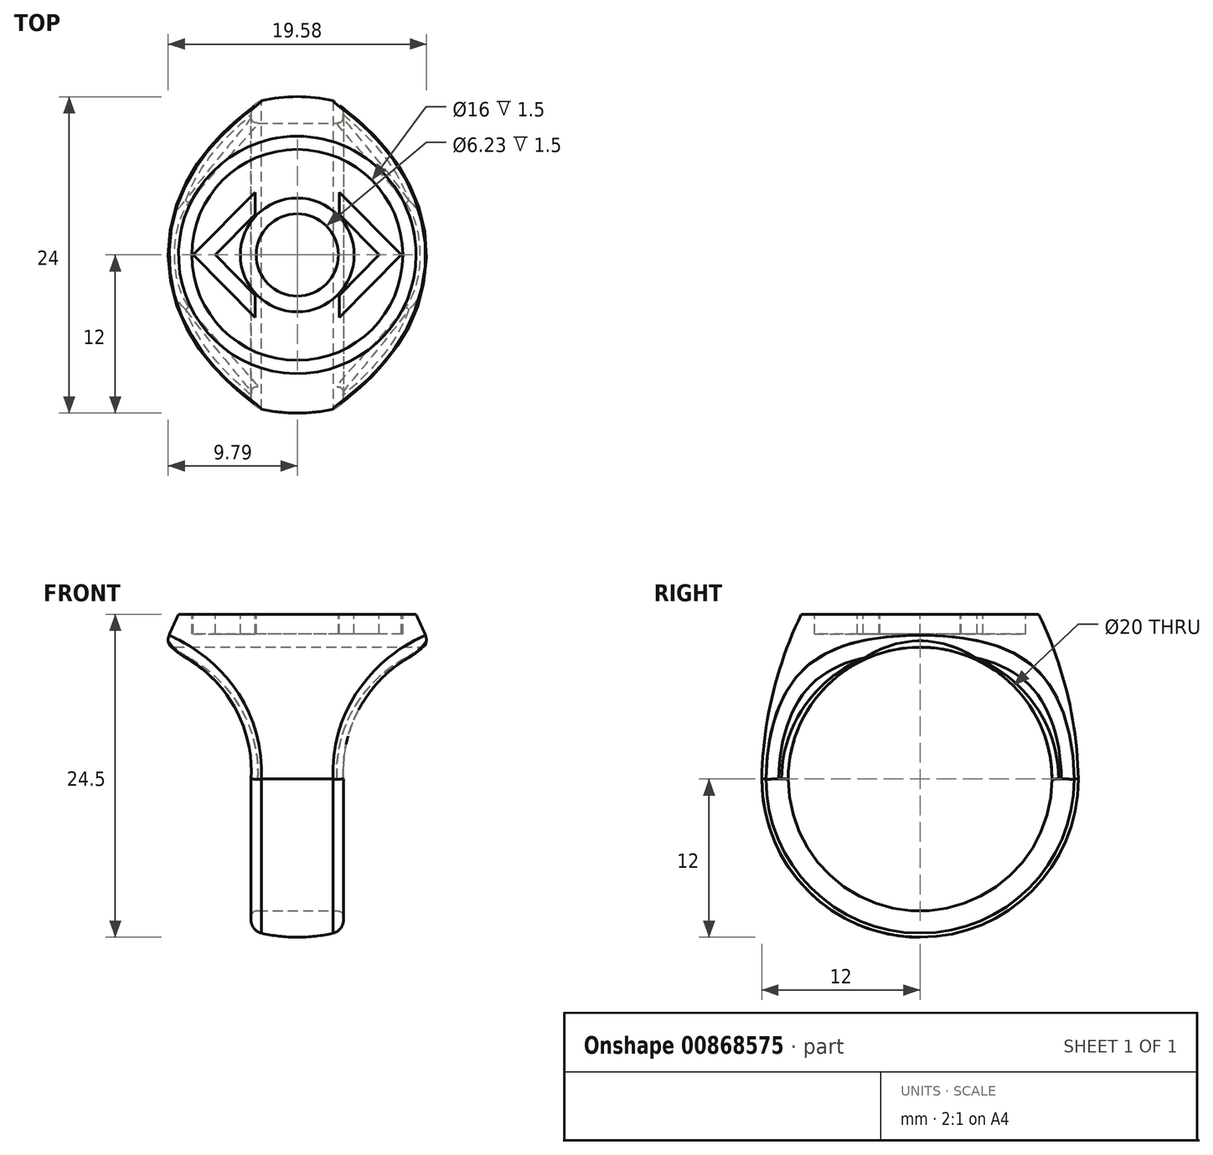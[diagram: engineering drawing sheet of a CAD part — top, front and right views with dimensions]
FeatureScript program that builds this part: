
annotation { "Feature Type Name" : "Feature", "Feature Type Description" : "" }
export const myFeature = defineFeature(function(context is Context, id is Id, definition is map)
    precondition{}
    {
        {
            var Q0;
            Q0=qCreatedBy(makeId("Right.planeOp"),FACE);
            var sketch = newSketch(context, id + "F0", { "sketchPlane" : qUnion([Q0])});
            skLineSegment(sketch, "E0", {"start": v(0, 0) * mm, "end": v(0, -24.5) * mm});
            skLineSegment(sketch, "E1", {"start": v(0, 0) * mm, "end": v(-9, 0) * mm});
            skArc(sketch, "E2", {"start": v(-12, -12.5) * mm, "mid": v(-8.49, -20.99) * mm, "end": v(0, -24.5) * mm});
            skLineSegment(sketch, "E3", {"start": v(0, -12.5) * mm, "end": v(-12, -12.5) * mm, "construction": true});
            skArc(sketch, "E4", {"start": v(-9, 0) * mm, "mid": v(-11.18, -6.09) * mm, "end": v(-12, -12.5) * mm});
            skSolve(sketch);
        }
        {
            var Q0;
            Q0=makeQuery(id+"F0.imprint","IMPRINT",FACE,{"disambiguationData":[TD([[makeQuery(id+"F0.imprint","IMPRINT",EDGE,{"derivedFrom":sQuery(id+"F0.wireOp",EDGE,"E0")}),-1.0]])]});
            var Q1;
            Q1=sQuery(id+"F0.wireOp",EDGE,"E0");
            revolve(context, id + "F1", {"entities" : qUnion([Q0]), "axis" : qUnion([Q1]), "revolveType" : RevolveType.FULL});
        }
        {
            var Q0;
            Q0=qCreatedBy(makeId("Right.planeOp"),FACE);
            var sketch = newSketch(context, id + "F2", { "sketchPlane" : qUnion([Q0])});
            skCircle(sketch, "E5", {"center": v(0, -12.5) * mm, "radius": 10 * mm});
            skSolve(sketch);
        }
        {
            var Q0;
            Q0=qSketchRegion(id+"F2",true);
            extrude(context, id + "F3", {"entities" : qUnion([Q0]), "operationType" : NewBodyOperationType.REMOVE, "endBound" : BoundingType.SYMMETRIC, "oppositeDirection" : true, "depth" : 25 * mm, "offsetDistance" : 25 * mm});
        }
        {
            var Q0;
            Q0=qCreatedBy(makeId("Front.planeOp"),FACE);
            var sketch = newSketch(context, id + "F4", { "sketchPlane" : qUnion([Q0])});
            skLineSegment(sketch, "E6", {"start": v(3.5, -26.5) * mm, "end": v(3.5, -12.5) * mm});
            skArc(sketch, "E7", {"start": v(10.15, -2.5) * mm, "mid": v(5.16, -6.39) * mm, "end": v(3.5, -12.5) * mm});
            skLineSegment(sketch, "E8", {"start": v(10.15, -2.5) * mm, "end": v(11.65, -2.5) * mm});
            skLineSegment(sketch, "E9", {"start": v(11.65, -2.5) * mm, "end": v(11.65, -26.5) * mm});
            skLineSegment(sketch, "E10", {"start": v(11.65, -26.5) * mm, "end": v(3.5, -26.5) * mm});
            skPoint(sketch, "E11.start.orphan", {"position": v(0, -24.5) * mm});
            skLineSegment(sketch, "E12", {"start": v(0, 0) * mm, "end": v(0, -24.5) * mm, "construction": true});
            skLineSegment(sketch, "E13.MirrorCS", {"start": v(-3.5, -26.5) * mm, "end": v(-3.5, -12.5) * mm});
            skArc(sketch, "E14.MirrorCS", {"start": v(-10.15, -2.5) * mm, "mid": v(-5.16, -6.39) * mm, "end": v(-3.5, -12.5) * mm});
            skLineSegment(sketch, "E15.MirrorCS", {"start": v(-11.65, -2.5) * mm, "end": v(-11.65, -26.5) * mm});
            skLineSegment(sketch, "E16.MirrorCS", {"start": v(-11.65, -26.5) * mm, "end": v(-3.5, -26.5) * mm});
            skLineSegment(sketch, "E17.MirrorCS", {"start": v(-10.15, -2.5) * mm, "end": v(-11.65, -2.5) * mm});
            skSolve(sketch);
        }
        {
            var Q0;
            Q0=qSketchRegion(id+"F4",true);
            extrude(context, id + "F5", {"entities" : qUnion([Q0]), "operationType" : NewBodyOperationType.REMOVE, "endBound" : BoundingType.SYMMETRIC, "depth" : 25 * mm, "offsetDistance" : 25 * mm});
        }
        {
            var Q0;
            Q0=makeQuery(id+"F1.opRevolve","SWEPT_FACE",FACE,{"disambiguationData":[OSD([sQuery(id+"F0.wireOp",EDGE,"E1")])]});
            var sketch = newSketch(context, id + "F6", { "sketchPlane" : qUnion([Q0])});
            skCircle(sketch, "E18", {"center": v(0, 0) * mm, "radius": 8 * mm});
            skLineSegment(sketch, "E19", {"start": v(-8, 0) * mm, "end": v(8, 0) * mm, "construction": true});
            skArc(sketch, "E20", {"start": v(3.11, 0) * mm, "mid": v(0, 3.11) * mm, "end": v(-3.11, 0) * mm});
            skArc(sketch, "E21", {"start": v(4.31, 0) * mm, "mid": v(0, 4.31) * mm, "end": v(-4.31, 0) * mm});
            skLineSegment(sketch, "E22", {"start": v(0, 8) * mm, "end": v(0, -8) * mm, "construction": true});
            skArc(sketch, "E23", {"start": v(4.31, 0) * mm, "mid": v(0, -4.31) * mm, "end": v(-4.31, 0) * mm});
            skArc(sketch, "E24", {"start": v(3.11, 0) * mm, "mid": v(0, -3.11) * mm, "end": v(-3.11, 0) * mm});
            skLineSegment(sketch, "E25", {"start": v(3.18, 4.76) * mm, "end": v(3.18, 3.05) * mm});
            skLineSegment(sketch, "E26", {"start": v(6.21, 0) * mm, "end": v(3.18, -3.05) * mm});
            skLineSegment(sketch, "E27", {"start": v(6.21, 0) * mm, "end": v(3.18, 3.05) * mm});
            skLineSegment(sketch, "E28.trimOffspring", {"start": v(3.18, -3.05) * mm, "end": v(3.18, -4.76) * mm});
            skLineSegment(sketch, "E29", {"start": v(3.18, -4.76) * mm, "end": v(7.9, 0) * mm});
            skLineSegment(sketch, "E30", {"start": v(7.9, 0) * mm, "end": v(3.18, 4.76) * mm});
            skLineSegment(sketch, "E31.MirrorCS", {"start": v(-3.18, 4.76) * mm, "end": v(-3.18, 3.05) * mm});
            skLineSegment(sketch, "E32.MirrorCS", {"start": v(-7.9, 0) * mm, "end": v(-3.18, 4.76) * mm});
            skLineSegment(sketch, "E33.MirrorCS", {"start": v(-6.21, 0) * mm, "end": v(-3.18, 3.05) * mm});
            skLineSegment(sketch, "E34.MirrorCS", {"start": v(-6.21, 0) * mm, "end": v(-3.18, -3.05) * mm});
            skLineSegment(sketch, "E35.MirrorCS", {"start": v(-3.18, -4.76) * mm, "end": v(-7.9, 0) * mm});
            skLineSegment(sketch, "E36.MirrorCS", {"start": v(-3.18, -3.05) * mm, "end": v(-3.18, -4.76) * mm});
            skSolve(sketch);
        }
        {
            var Q0;
            Q0=makeQuery(id+"F6.imprint","IMPRINT",FACE,{"disambiguationData":[TD([[makeQuery(id+"F6.imprint","IMPRINT",EDGE,{"derivedFrom":sQuery(id+"F6.wireOp",EDGE,"E20")}),1.0]])]});
            var Q1;
            Q1=makeQuery(id+"F6.imprint","IMPRINT",FACE,{"disambiguationData":[TD([[makeQuery(id+"F6.imprint","IMPRINT",EDGE,{"derivedFrom":sQuery(id+"F6.wireOp",EDGE,"E18")}),1.0]])]});
            extrude(context, id + "F7", {"entities" : qUnion([Q0, Q1]), "operationType" : NewBodyOperationType.REMOVE, "oppositeDirection" : true, "depth" : 1.5 * mm, "offsetDistance" : 25 * mm});
        }
        {
            var Q0;
            Q0=makeQuery(id+"F5.boolean.opBoolean","INTERSECT",EDGE,{"disambiguationData":[OD(1.0)],"derivedFrom":[makeQuery(id+"F1.opRevolve","SWEPT_FACE",FACE,{"disambiguationData":[OSD([sQuery(id+"F0.wireOp",EDGE,"E4")])]}),makeQuery(id+"F5.opExtrude","SWEPT_FACE",FACE,{"disambiguationData":[OSD([sQuery(id+"F4.wireOp",EDGE,"E14.MirrorCS")])]})]});
            var Q1;
            Q1=makeQuery(id+"F5.boolean.opBoolean","INTERSECT",EDGE,{"derivedFrom":[makeQuery(id+"F1.opRevolve","SWEPT_FACE",FACE,{"disambiguationData":[OSD([sQuery(id+"F0.wireOp",EDGE,"E2")])]}),makeQuery(id+"F5.opExtrude","SWEPT_FACE",FACE,{"disambiguationData":[OSD([sQuery(id+"F4.wireOp",EDGE,"E13.MirrorCS")])]})]});
            var Q2;
            Q2=makeQuery(id+"F5.boolean.opBoolean","INTERSECT",EDGE,{"disambiguationData":[OD(1.0)],"derivedFrom":[makeQuery(id+"F1.opRevolve","SWEPT_FACE",FACE,{"disambiguationData":[OSD([sQuery(id+"F0.wireOp",EDGE,"E4")])]}),makeQuery(id+"F5.opExtrude","SWEPT_FACE",FACE,{"disambiguationData":[OSD([sQuery(id+"F4.wireOp",EDGE,"E7")])]})]});
            var Q3;
            Q3=makeQuery(id+"F5.boolean.opBoolean","INTERSECT",EDGE,{"derivedFrom":[makeQuery(id+"F1.opRevolve","SWEPT_FACE",FACE,{"disambiguationData":[OSD([sQuery(id+"F0.wireOp",EDGE,"E2")])]}),makeQuery(id+"F5.opExtrude","SWEPT_FACE",FACE,{"disambiguationData":[OSD([sQuery(id+"F4.wireOp",EDGE,"E6")])]})]});
            fillet(context, id + "F8", {"entities" : qUnion([Q0, Q1, Q2, Q3]), "radius" : 1 * mm, "allowEdgeOverflow" : false});
        }
        {
            var Q0;
            Q0=makeQuery(id+"F5.boolean.opBoolean","INTERSECT",EDGE,{"disambiguationData":[OD(1.0)],"derivedFrom":[makeQuery(id+"F3.boolean.opBoolean","COPY",FACE,{"derivedFrom":makeQuery(id+"F3.opExtrude","SWEPT_FACE",FACE,{"disambiguationData":[OSD([sQuery(id+"F2.wireOp",EDGE,"E5")])]})}),makeQuery(id+"F5.opExtrude","SWEPT_FACE",FACE,{"disambiguationData":[OSD([sQuery(id+"F4.wireOp",EDGE,"E14.MirrorCS")])]})]});
            var Q1;
            Q1=makeQuery(id+"F5.boolean.opBoolean","INTERSECT",EDGE,{"derivedFrom":[makeQuery(id+"F3.boolean.opBoolean","COPY",FACE,{"derivedFrom":makeQuery(id+"F3.opExtrude","SWEPT_FACE",FACE,{"disambiguationData":[OSD([sQuery(id+"F2.wireOp",EDGE,"E5")])]})}),makeQuery(id+"F5.opExtrude","SWEPT_FACE",FACE,{"disambiguationData":[OSD([sQuery(id+"F4.wireOp",EDGE,"E13.MirrorCS")])]})]});
            var Q2;
            Q2=makeQuery(id+"F5.boolean.opBoolean","INTERSECT",EDGE,{"disambiguationData":[OD(0.0)],"derivedFrom":[makeQuery(id+"F3.boolean.opBoolean","COPY",FACE,{"derivedFrom":makeQuery(id+"F3.opExtrude","SWEPT_FACE",FACE,{"disambiguationData":[OSD([sQuery(id+"F2.wireOp",EDGE,"E5")])]})}),makeQuery(id+"F5.opExtrude","SWEPT_FACE",FACE,{"disambiguationData":[OSD([sQuery(id+"F4.wireOp",EDGE,"E14.MirrorCS")])]})]});
            var Q3;
            Q3=makeQuery(id+"F5.boolean.opBoolean","INTERSECT",EDGE,{"disambiguationData":[OD(0.0)],"derivedFrom":[makeQuery(id+"F3.boolean.opBoolean","COPY",FACE,{"derivedFrom":makeQuery(id+"F3.opExtrude","SWEPT_FACE",FACE,{"disambiguationData":[OSD([sQuery(id+"F2.wireOp",EDGE,"E5")])]})}),makeQuery(id+"F5.opExtrude","SWEPT_FACE",FACE,{"disambiguationData":[OSD([sQuery(id+"F4.wireOp",EDGE,"E7")])]})]});
            var Q4;
            Q4=makeQuery(id+"F3.boolean.opBoolean","COPY",FACE,{"derivedFrom":makeQuery(id+"F3.opExtrude","SWEPT_FACE",FACE,{"disambiguationData":[OSD([sQuery(id+"F2.wireOp",EDGE,"E5")])]})});
            fillet(context, id + "F9", {"entities" : qUnion([Q0, Q1, Q2, Q3, Q4]), "radius" : .5 * mm, "rho" : 0.5, "crossSection" : FilletCrossSection.CONIC, "allowEdgeOverflow" : false});
        }
    });
